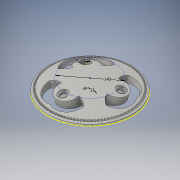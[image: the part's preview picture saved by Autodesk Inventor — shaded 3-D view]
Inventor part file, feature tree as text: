
AUTODESK INVENTOR PART (.ipt)
format: ipt  version: 2016 (Build 200138000, 138)  size: 717,312 bytes
history: native  units: in
note: dims shown in document units (in); Inventor stores cm internally (conversion verified against a paired STEP export)
features: sketch x14, extrude x8, plane x5, pattern_circular x4, revolve x1, hole x1, fillet x1
ambient origin geometry x8: Origin, YZ Plane, XZ Plane, XY Plane, X Axis, Y Axis, Z Axis, Center Point
bodies: Solid1 (feature_tree)
feature tree (34):
  revolve  "Revolution1"  [1 undecoded]
  sketch  "Sketch8"  dims[d2=0.2405in d23=0.1575in]
  plane  "Work Plane4"
  plane  "Work Plane5"
  extrude  "Extrusion6"  Depth=0.1575in
  pattern_circular  "Circular Pattern1"  Count=100 Angle=360.0deg
  plane  "Work Plane7"
  sketch  "Sketch15"  dims[d25=0.1718in d26=-0.1772in]
  sketch  "Sketch16"  dims[d27=-1.3125in]
  sketch  "Sketch17"  dims[d31=0.6411in]
  extrude  "Extrusion7"  Depth=5.5118in
  extrude  "Extrusion8"  Depth=7.1323in
  pattern_circular  "Circular Pattern2"  Count=3 Angle=360.0deg
  sketch  "Sketch18"  dims[d32=0.2165in]
  sketch  "Sketch20"  dims[d33=0.315in d34=0.0in d35=39.3701in d36=360.0deg]
  extrude  "Extrusion9"  Depth=0.9843in
  sketch  "Sketch22"  dims[d44=7.1754in d45=7.1323in]
  extrude  "Extrusion11"  Depth=0.3543in
  hole  "Hole1"  [1 undecoded]
  pattern_circular  "Circular Pattern3"  [2 undecoded]
  extrude  "Extrusion19"  Depth=0.0079in TaperAngle=0.0deg
  pattern_circular  "Circular Pattern4"  [2 undecoded]
  extrude  "Extrusion22"  Depth=0.0787in
  extrude  "Extrusion23"  Depth=1.1811in TaperAngle=0.0deg
  fillet  "Fillet2"  Radius=0.0787in
  sketch  "Sketch1"  dims[d0=20.0in d1=9.293in]
  plane  "Work Plane3"
  sketch  "Sketch10"  dims[d24=0.9843in]
  plane  "Work Plane6"
  sketch  "Sketch21"  dims[d41=15.0deg d42=-0.4134in d43=5.5118in]
  sketch  "Sketch26"  dims[d46=0.9843in]
  sketch  "Sketch38"  dims[d47=0.6693in]
  sketch  "Sketch43"  dims[d48=0.1181in d49=0.0in]
  sketch  "Sketch44"  dims[d50=0.3543in d51=0.0in d52=1.1811in d53=360.0deg d60=0.9843in d61=0.3543in d62=0.315in d63=0.315in d64=0.0079in d65=0.0in d66=0.9843in d67=0.1181in d74=1.1811in d75=0.0in d76=0.0787in d77=1.1811in d79=360.0deg d81=0.0787in d82=0.2362in d83=0.1575in d84=0.0787in d85=90.0deg d86=0.3937in d87=0.8108in d88=1.1811in d89=360.0deg d107=3.2436in d108=0.0in d109=1.1811in d110=360.0deg d116=0.9843in d117=0.0in d118=0.9843in d119=0.1181in d120=0.9843in d121=0.0in d122=0.0787in]
note: 6 required parameter values undecoded (feature->parameter linkage not recoverable at this tier; creation-order binding heuristic only, values carry confidence <= 0.55)